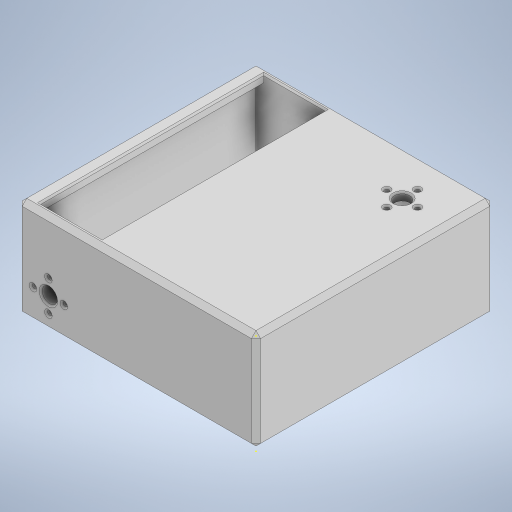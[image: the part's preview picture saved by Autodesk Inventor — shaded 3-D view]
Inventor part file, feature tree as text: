
AUTODESK INVENTOR PART (.ipt)
format: ipt  version: 2023 (Build 270158000, 158)  size: 331,264 bytes
history: native  units: mm
features: sketch x23, extrude x10, chamfer x5
ambient origin geometry x8: Origin, YZ Plane, XZ Plane, XY Plane, X Axis, Y Axis, Z Axis, Center Point
bodies: Solid1 (feature_tree)
feature tree (38):
  extrude  "Extrusion1"  Depth=155.0mm
  extrude  "Extrusion2"  Depth=5.0mm
  extrude  "Extrusion3"  Depth=5.0mm
  extrude  "Extrusion4"  Depth=55.0mm TaperAngle=0.0deg
  extrude  "Extrusion5"  Depth=10.0mm
  extrude  "Extrusion6"  Depth=30.0mm
  extrude  "Extrusion7"  Depth=5.0mm
  sketch  "Sketch8"  dims[d18=20.0mm]
  sketch  "Sketch9"  dims[d19=10.0mm d20=20.0mm d21=0.0mm]
  sketch  "Sketch10"  dims[d22=10.0mm]
  chamfer  "Chamfer1"  Distance=20.0mm
  chamfer  "Chamfer3"  Distance=5.0mm
  extrude  "Extrusion9"  Depth=40.0mm TaperAngle=360.0deg
  sketch  "Sketch13"  dims[d24=5.0mm]
  extrude  "Extrusion10"  Depth=10.0mm
  chamfer  "Chamfer4"  Distance=2.0mm Angle=45.0deg
  chamfer  "Chamfer5"  Distance=2.0mm Angle=45.0deg
  sketch  "Sketch15"  dims[d28=3.0mm d29=40.0mm d31=360.0deg]
  sketch  "Sketch16"  dims[d33=5.0mm d34=0.0mm d35=10.0mm d44=1.0mm d45=2.0mm d46=45.0deg d50=1.0mm d51=2.0mm d52=45.0deg]
  sketch  "Sketch17"  dims[d53=30.0mm d54=30.0mm d55=5.0mm d56=0.0mm]
  sketch  "Sketch18"  dims[d57=20.0mm d58=0.0mm]
  sketch  "Sketch19"  dims[d59=1.0mm d60=2.0mm d61=45.0deg]
  sketch  "Sketch20"  dims[d62=3.0mm d63=2.0mm d64=45.0deg]
  sketch  "Sketch21"  dims[d66=3.0mm]
  sketch  "Sketch22"  dims[d67=10.0mm]
  sketch  "Sketch23"  dims[d68=40.0mm d70=360.0deg]
  extrude  "Extrusion11"  Depth=30.0mm
  chamfer  "Chamfer6"  Distance=5.0mm
  sketch  "Sketch24"  dims[d72=10.0mm d73=0.0mm d74=1.0mm d75=2.0mm d76=45.0deg d30=0.872665mm d32=0.872665mm]
  sketch  "Sketch1"  dims[d0=155.0mm d1=155.0mm]
  sketch  "Sketch2"  dims[d2=60.0mm d3=0.0mm d4=5.0mm]
  sketch  "Sketch3"  dims[d5=5.0mm d6=5.0mm]
  sketch  "Sketch4"  dims[d7=5.0mm d8=55.0mm d9=0.0mm]
  sketch  "Sketch5"  dims[d10=5.0mm d11=0.0mm d12=10.0mm]
  sketch  "Sketch6"  dims[d13=30.0mm d14=30.0mm]
  sketch  "Sketch7"  dims[d15=5.0mm d16=0.0mm d17=20.0mm]
  sketch  "Sketch12"  dims[d23=5.0mm]
  sketch  "Sketch14"  dims[d25=40.0mm d26=5.0mm d27=0.0mm]
